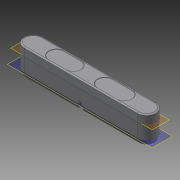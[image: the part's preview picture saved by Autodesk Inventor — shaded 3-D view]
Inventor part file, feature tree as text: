
AUTODESK INVENTOR PART (.ipt)
format: ipt  version: 2014 (Build 180170000, 170)  size: 207,360 bytes
history: native  units: mm
features: extrude x5, sketch x5, other x4, chamfer x2, plane x2, fillet x1
ambient origin geometry x8: Origin, YZ Plane, XZ Plane, XY Plane, X Axis, Y Axis, Z Axis, Center Point
bodies: Volumenkörper1 (feature_tree)
feature tree (19):
  extrude  "Extrusion1"  Depth=25.0mm
  fillet  "Rundung1"  Radius=36.0mm
  chamfer  "Fase1"  Distance=2.0mm
  plane  "Arbeitsebene1"
  plane  "Arbeitsebene2"
  other  "Trennen1"
  other  "Flächenverjüngung1"
  other  "Trennen3"
  other  "Flächenverjüngung3"
  extrude  "Extrusion2"  [1 undecoded]
  extrude  "Extrusion3"  Depth=0.174533mm
  extrude  "Extrusion4"  Depth=0.5mm
  extrude  "Extrusion5"  Depth=0.5mm
  chamfer  "Fase2"  Distance=1.0mm
  sketch  "Skizze1"  dims[d0=178.0mm d1=25.0mm d2=36.0mm d3=0.0mm]
  sketch  "Skizze2"  dims[d4=12.5mm d5=2.0mm d6=2.0mm d7=3.490659mm]
  sketch  "Skizze3"  dims[d8=-11.0mm d9=-6.0mm]
  sketch  "Skizze4"  dims[d10=0.174533mm d12=2.96706mm]
  sketch  "Skizze5"  dims[d13=6.0mm d14=6.0mm d15=1.0mm d16=1.0mm d17=23.0mm d18=0.0mm d19=6.0mm d21=82.0mm d22=10.0mm d23=0.0mm d24=3.0mm d25=3.0mm d26=3.0mm d27=3.0mm d28=19.5mm d29=33.5mm d30=36.0mm d31=0.2mm d32=0.0mm d33=44.0mm d34=47.0mm d35=22.0mm d36=31.0mm d37=21.0mm d38=10.5mm d39=0.5mm d40=0.0mm d41=0.5mm d42=2.0mm d43=45.0deg]
note: 1 required parameter value undecoded (feature->parameter linkage not recoverable at this tier; creation-order binding heuristic only, values carry confidence <= 0.55)
